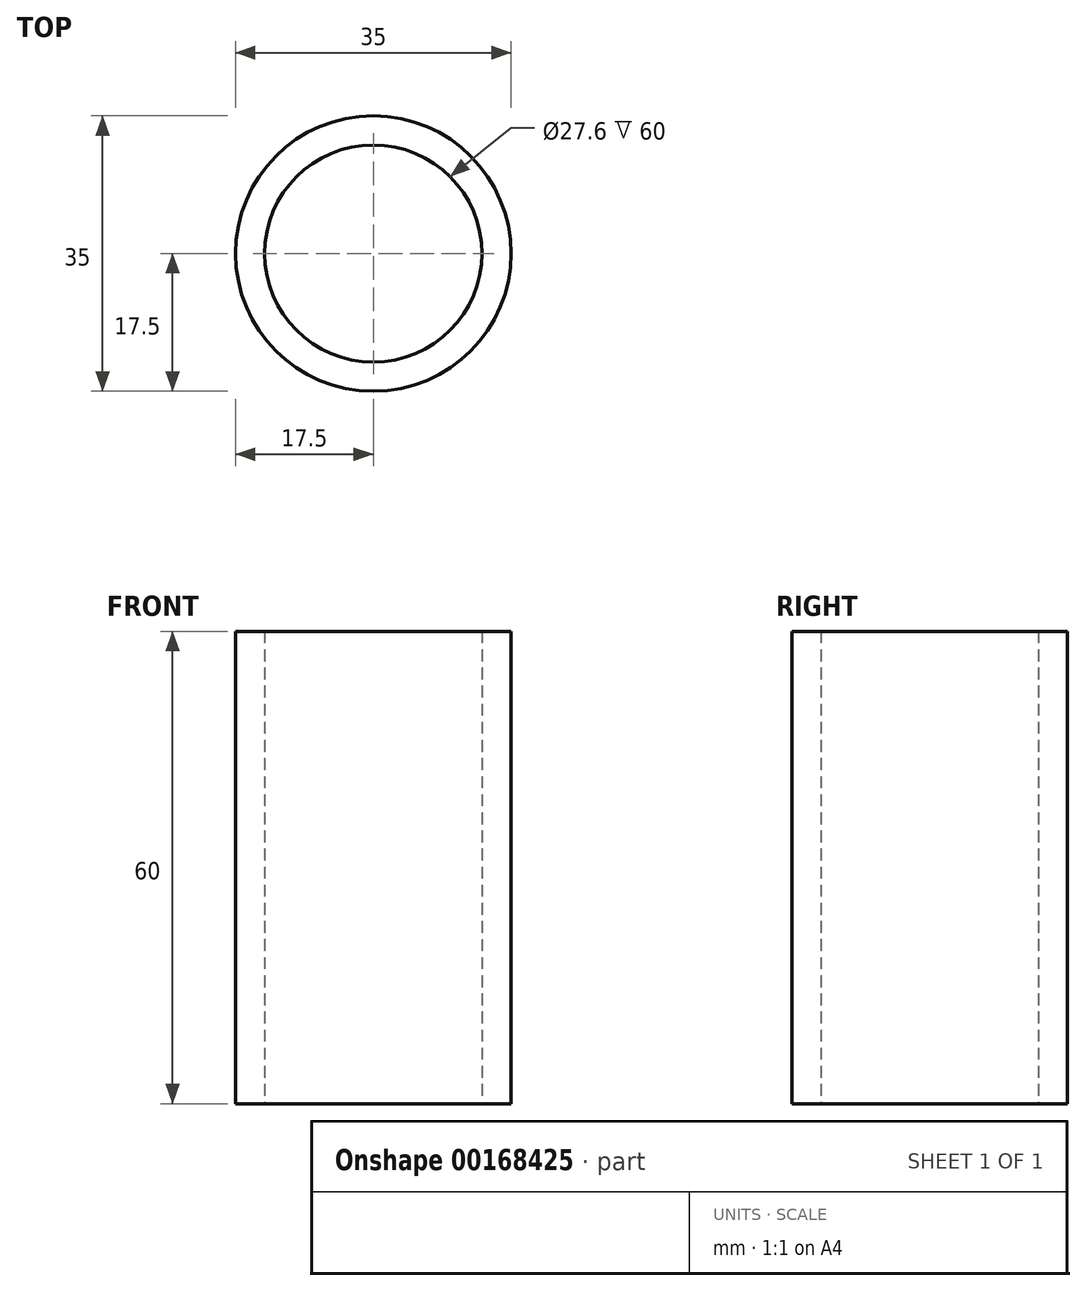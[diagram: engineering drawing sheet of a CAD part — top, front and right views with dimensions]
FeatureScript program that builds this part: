
annotation { "Feature Type Name" : "Feature", "Feature Type Description" : "" }
export const myFeature = defineFeature(function(context is Context, id is Id, definition is map)
    precondition{}
    {
        {
            var Q0;
            Q0=qCreatedBy(makeId("Top.planeOp"),FACE);
            var sketch = newSketch(context, id + "F0", { "sketchPlane" : qUnion([Q0])});
            skCircle(sketch, "E0", {"center": v(0, 0) * mm, "radius": 13.8 * mm});
            skCircle(sketch, "E1", {"center": v(0, 0) * mm, "radius": 17.5 * mm});
            skSolve(sketch);
        }
        {
            var Q0;
            Q0=makeQuery(id+"F0.imprint","IMPRINT",FACE,{"disambiguationData":[TD([[makeQuery(id+"F0.imprint","IMPRINT",EDGE,{"derivedFrom":sQuery(id+"F0.wireOp",EDGE,"E0")}),-1.0]])]});
            extrude(context, id + "F1", {"entities" : qUnion([Q0]), "depth" : 60 * mm});
        }
    });
